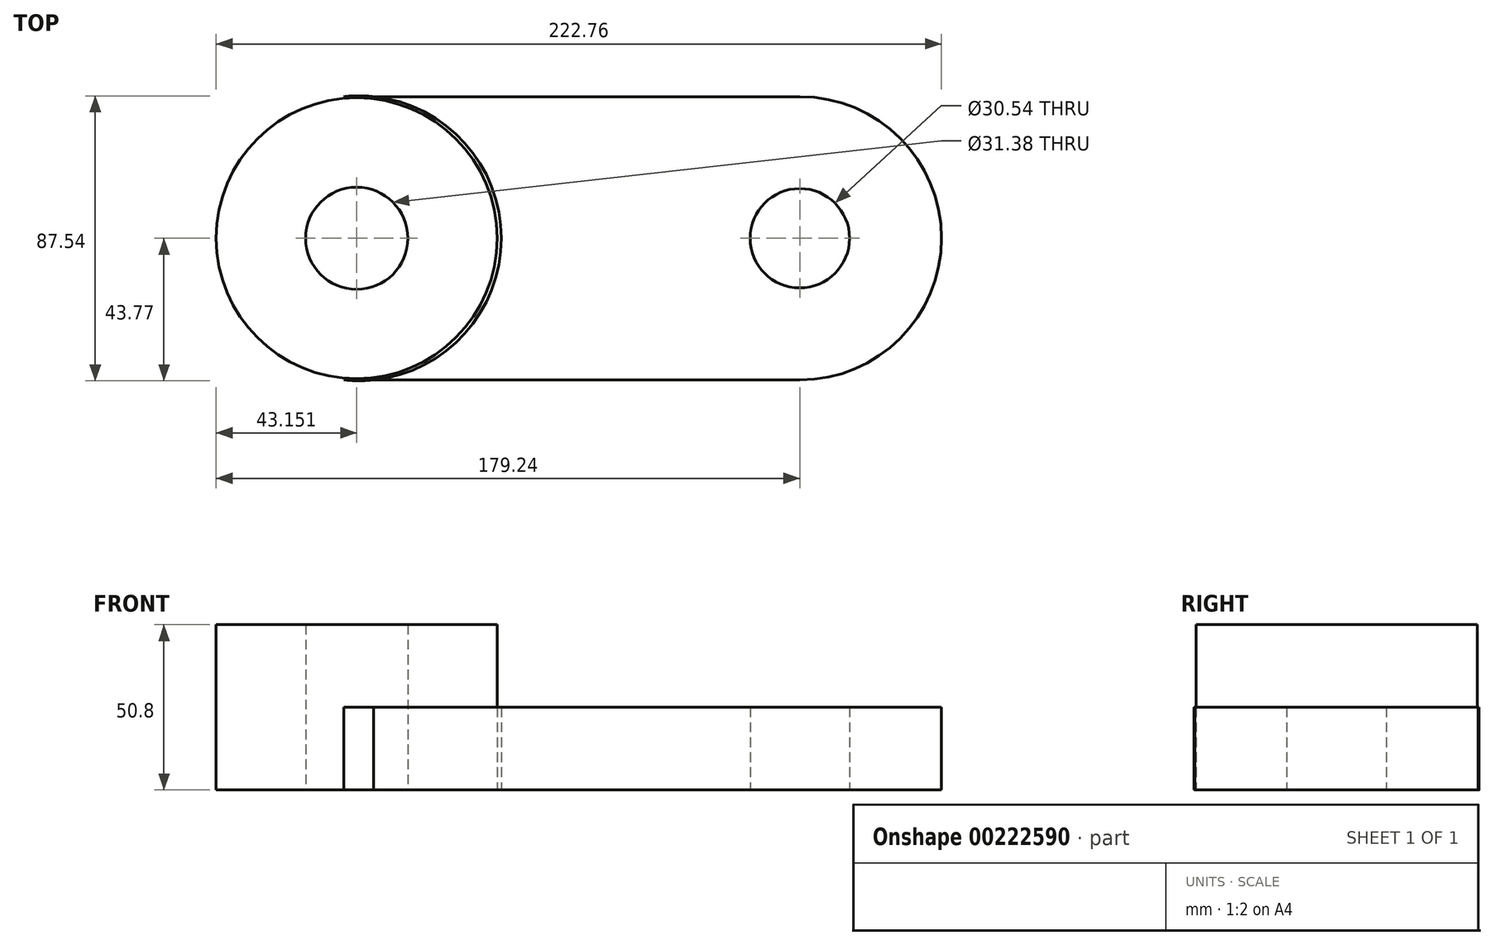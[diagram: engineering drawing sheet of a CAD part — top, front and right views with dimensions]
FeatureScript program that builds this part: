
annotation { "Feature Type Name" : "Feature", "Feature Type Description" : "" }
export const myFeature = defineFeature(function(context is Context, id is Id, definition is map)
    precondition{}
    {
        {
            var Q0;
            Q0=qCreatedBy(makeId("Top.planeOp"),FACE);
            var sketch = newSketch(context, id + "F0", { "sketchPlane" : qUnion([Q0])});
            skCircle(sketch, "E0", {"center": v(-66.72, 0) * mm, "radius": 43.15 * mm});
            skCircle(sketch, "E1", {"center": v(-66.72, 0) * mm, "radius": 15.7 * mm});
            skSolve(sketch);
        }
        {
            var Q0;
            Q0=makeQuery(id+"F0.imprint","IMPRINT",FACE,{"disambiguationData":[TD([[makeQuery(id+"F0.imprint","IMPRINT",EDGE,{"derivedFrom":sQuery(id+"F0.wireOp",EDGE,"E0")}),1.0]])]});
            extrude(context, id + "F1", {"entities" : qUnion([Q0]), "depth" : 50.8 * mm});
        }
        {
            var Q0;
            Q0=qCreatedBy(makeId("Top.planeOp"),FACE);
            var sketch = newSketch(context, id + "F2", { "sketchPlane" : qUnion([Q0])});
            skLineSegment(sketch, "E2", {"start": v(-70.7, 43.52) * mm, "end": v(69.37, 43.52) * mm});
            skLineSegment(sketch, "E3", {"start": v(-70.7, -43.52) * mm, "end": v(69.37, -43.52) * mm});
            skArc(sketch, "E4", {"start": v(-70.7, -43.52) * mm, "mid": v(-22.32, 0) * mm, "end": v(-70.7, 43.52) * mm});
            skArc(sketch, "E5", {"start": v(69.37, -43.52) * mm, "mid": v(112.9, 0) * mm, "end": v(69.37, 43.52) * mm});
            skCircle(sketch, "E6", {"center": v(69.37, 0) * mm, "radius": 15.27 * mm});
            skSolve(sketch);
        }
        {
            var Q0;
            Q0 = qSketchRegion(id + "F2", true);
            var Q1;
            {var subQ0=sQuery(id+"F2.wireOp",EDGE,"E5");Q1=makeQuery(id+"F2.imprint","IMPRINT",FACE,{"disambiguationData":[TD([[makeQuery(id+"F2.imprint","IMPRINT",EDGE,{"derivedFrom":subQ0}),1.0]])]});}
            extrude(context, id + "F3", {"entities" : qUnion([Q0, Q1]), "depth" : 25.4 * mm});
        }
    });
